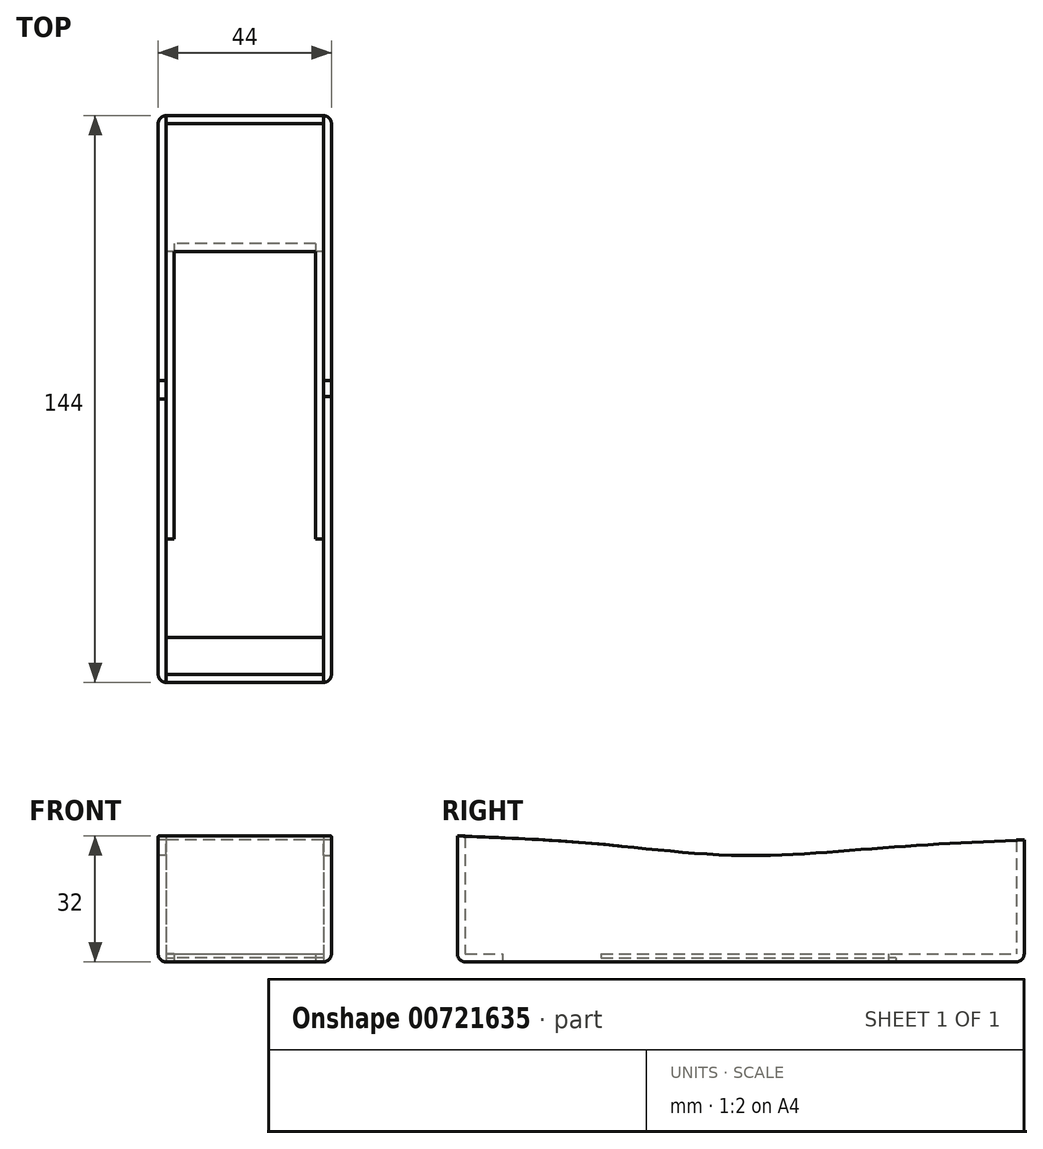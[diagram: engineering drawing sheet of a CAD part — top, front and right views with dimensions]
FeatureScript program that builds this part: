
annotation { "Feature Type Name" : "Feature", "Feature Type Description" : "" }
export const myFeature = defineFeature(function(context is Context, id is Id, definition is map)
    precondition{}
    {
        {
            var Q0;
            Q0=qCreatedBy(makeId("Top.planeOp"),FACE);
            var sketch = newSketch(context, id + "F0", { "sketchPlane" : qUnion([Q0])});
            skLineSegment(sketch, "E0.bottom", {"start": v(20, -70) * mm, "end": v(-20, -70) * mm});
            skLineSegment(sketch, "E0.top", {"start": v(20, 70) * mm, "end": v(-20, 70) * mm});
            skLineSegment(sketch, "E0.left", {"start": v(20, -70) * mm, "end": v(20, 70) * mm});
            skLineSegment(sketch, "E0.right", {"start": v(-20, -70) * mm, "end": v(-20, 70) * mm});
            skPoint(sketch, "E0.middle", {"position": v(0, 0) * mm});
            skLineSegment(sketch, "E1.bottom", {"start": v(22, -72) * mm, "end": v(-22, -72) * mm});
            skLineSegment(sketch, "E1.top", {"start": v(22, 72) * mm, "end": v(-22, 72) * mm});
            skLineSegment(sketch, "E1.left", {"start": v(22, -72) * mm, "end": v(22, 72) * mm});
            skLineSegment(sketch, "E1.right", {"start": v(-22, -72) * mm, "end": v(-22, 72) * mm});
            skSolve(sketch);
        }
        {
            var Q0;
            Q0=makeQuery(id+"F0.imprint","IMPRINT",FACE,{"disambiguationData":[TD([[makeQuery(id+"F0.imprint","IMPRINT",EDGE,{"derivedFrom":sQuery(id+"F0.wireOp",EDGE,"E0.bottom")}),1.0]])]});
            var Q1;
            Q1=makeQuery(id+"F0.imprint","IMPRINT",FACE,{"disambiguationData":[TD([[makeQuery(id+"F0.imprint","IMPRINT",EDGE,{"derivedFrom":sQuery(id+"F0.wireOp",EDGE,"E0.bottom")}),-1.0]])]});
            extrude(context, id + "F1", {"entities" : qUnion([Q0, Q1]), "oppositeDirection" : true, "depth" : 2 * mm, "offsetDistance" : 25 * mm});
        }
        {
            var Q0;
            Q0=makeQuery(id+"F0.imprint","IMPRINT",FACE,{"disambiguationData":[TD([[makeQuery(id+"F0.imprint","IMPRINT",EDGE,{"derivedFrom":sQuery(id+"F0.wireOp",EDGE,"E0.bottom")}),1.0]])]});
            extrude(context, id + "F2", {"entities" : qUnion([Q0]), "operationType" : NewBodyOperationType.ADD, "depth" : 25 * mm, "offsetDistance" : 25 * mm});
        }
        {
            var Q0;
            {var subQ0=sQuery(id+"F0.wireOp",EDGE,"E1.left");Q0=makeQuery(id+"F2.boolean.opBoolean","MERGE",FACE,{"derivedFrom":[makeQuery(id+"F1.opExtrude","SWEPT_FACE",FACE,{"disambiguationData":[OSD([subQ0])]}),makeQuery(id+"F2.opExtrude","SWEPT_FACE",FACE,{"disambiguationData":[OSD([subQ0])]})]});}
            var sketch = newSketch(context, id + "F3", { "sketchPlane" : qUnion([Q0])});
            skLineSegment(sketch, "E2", {"start": v(-72, 25) * mm, "end": v(-72, 30) * mm});
            skLineSegment(sketch, "E3", {"start": v(72, 25) * mm, "end": v(72, 29) * mm});
            skLineSegment(sketch, "E4", {"start": v(0, 25) * mm, "end": v(0, 25.01) * mm, "construction": true});
            skLineSegment(sketch, "E5", {"start": v(-36.5, 25) * mm, "end": v(-36.5, 28) * mm, "construction": true});
            skLineSegment(sketch, "E6", {"start": v(36.5, 25) * mm, "end": v(36.5, 27) * mm, "construction": true});
            skFitSpline(sketch, "E7", {"points": [v(-72, 30) * mm, v(-36.5, 28) * mm, v(0, 25.01) * mm, v(36.5, 27) * mm, v(72, 29) * mm], "startDerivative": vector(142.08, -5.52) * mm, "endDerivative": vector(142.02, 6.52) * mm});
            skSolve(sketch);
        }
        {
            var Q0;
            {var subQ0=sQuery(id+"F0.wireOp",EDGE,"E1.right");Q0=makeQuery(id+"F2.boolean.opBoolean","MERGE",FACE,{"derivedFrom":[makeQuery(id+"F1.opExtrude","SWEPT_FACE",FACE,{"disambiguationData":[OSD([subQ0])]}),makeQuery(id+"F2.opExtrude","SWEPT_FACE",FACE,{"disambiguationData":[OSD([subQ0])]})]});}
            var sketch = newSketch(context, id + "F4", { "sketchPlane" : qUnion([Q0])});
            skLineSegment(sketch, "E8", {"start": v(72, 25) * mm, "end": v(72, 30) * mm});
            skLineSegment(sketch, "E9", {"start": v(-72, 25) * mm, "end": v(-72, 29) * mm});
            skLineSegment(sketch, "E10", {"start": v(-36.5, 25) * mm, "end": v(-36.5, 27) * mm, "construction": true});
            skLineSegment(sketch, "E11", {"start": v(36.5, 25) * mm, "end": v(36.5, 28) * mm, "construction": true});
            skLineSegment(sketch, "E12", {"start": v(0, 25) * mm, "end": v(0, 25.01) * mm});
            skFitSpline(sketch, "E13", {"points": [v(-72, 29) * mm, v(-36.5, 27) * mm, v(0, 25.01) * mm, v(36.5, 28) * mm, v(72, 30) * mm], "startDerivative": vector(142.02, -6.52) * mm, "endDerivative": vector(142.08, 5.52) * mm});
            skSolve(sketch);
        }
        {
            var Q0;
            {var subQ0=sQuery(id+"F3.wireOp",EDGE,"E3");Q0=makeQuery(id+"F3.imprint","IMPRINT",FACE,{"disambiguationData":[TD([[makeQuery(id+"F3.imprint","IMPRINT",EDGE,{"derivedFrom":subQ0}),1.0]])]});}
            var Q1;
            {var subQ0=sQuery(id+"F3.wireOp",EDGE,"E2");Q1=makeQuery(id+"F3.imprint","IMPRINT",FACE,{"disambiguationData":[TD([[makeQuery(id+"F3.imprint","IMPRINT",EDGE,{"derivedFrom":subQ0}),-1.0]])]});}
            extrude(context, id + "F5", {"entities" : qUnion([Q0, Q1]), "operationType" : NewBodyOperationType.ADD, "oppositeDirection" : true, "depth" : 2 * mm, "offsetDistance" : 25 * mm});
        }
        {
            var Q0;
            Q0 = qSketchRegion(id + "F4", true);
            var Q1;
            {var subQ0=sQuery(id+"F4.wireOp",EDGE,"E9");Q1=makeQuery(id+"F4.imprint","IMPRINT",FACE,{"disambiguationData":[TD([[makeQuery(id+"F4.imprint","IMPRINT",EDGE,{"derivedFrom":subQ0}),-1.0]])]});}
            var Q2;
            {var subQ0=sQuery(id+"F4.wireOp",EDGE,"E8");Q2=makeQuery(id+"F4.imprint","IMPRINT",FACE,{"disambiguationData":[TD([[makeQuery(id+"F4.imprint","IMPRINT",EDGE,{"derivedFrom":subQ0}),1.0]])]});}
            extrude(context, id + "F6", {"entities" : qUnion([Q0, Q1, Q2]), "operationType" : NewBodyOperationType.ADD, "oppositeDirection" : true, "depth" : 2 * mm, "offsetDistance" : 25 * mm});
        }
        {
            var Q0;
            {var subQ2=sQuery(id+"F0.wireOp",EDGE,"E1.right");var subQ3=sQuery(id+"F0.wireOp",EDGE,"E0.right");var subQ7=sQuery(id+"F0.wireOp",EDGE,"E1.bottom");var subQ11=sQuery(id+"F0.wireOp",EDGE,"E1.left");var subQ13=makeQuery(id+"F1.opExtrude","SWEPT_FACE",FACE,{"disambiguationData":[OSD([subQ7])]});var subQ15=sQuery(id+"F0.wireOp",EDGE,"E0.left");var subQ17=sQuery(id+"F0.wireOp",EDGE,"E0.bottom");var subQ19=sQuery(id+"F0.wireOp",EDGE,"E0.top");var subQ20=sQuery(id+"F0.wireOp",EDGE,"E1.top");Q0=makeQuery(id+"F6.boolean.opBoolean","SPLIT",FACE,{"disambiguationData":[TD([subQ13])],"derivedFrom":makeQuery(id+"F5.boolean.opBoolean","SPLIT",FACE,{"disambiguationData":[TD([subQ13])],"derivedFrom":makeQuery(id+"F2.opExtrude","CAP_FACE",FACE,{"disambiguationData":[OSD([subQ17,subQ19,subQ15,subQ3,subQ7,subQ20,subQ11,subQ2])],"isStart":false})})});}
            extrude(context, id + "F7", {"entities" : qUnion([Q0]), "operationType" : NewBodyOperationType.ADD, "depth" : 5 * mm, "offsetDistance" : 25 * mm});
        }
        {
            var Q0;
            {var subQ2=sQuery(id+"F0.wireOp",EDGE,"E1.right");var subQ3=sQuery(id+"F0.wireOp",EDGE,"E0.right");var subQ7=sQuery(id+"F0.wireOp",EDGE,"E1.left");var subQ9=sQuery(id+"F0.wireOp",EDGE,"E1.top");var subQ11=makeQuery(id+"F1.opExtrude","SWEPT_FACE",FACE,{"disambiguationData":[OSD([subQ9])]});var subQ12=sQuery(id+"F0.wireOp",EDGE,"E0.top");var subQ16=sQuery(id+"F0.wireOp",EDGE,"E0.left");var subQ19=sQuery(id+"F0.wireOp",EDGE,"E1.bottom");var subQ20=sQuery(id+"F0.wireOp",EDGE,"E0.bottom");Q0=makeQuery(id+"F6.boolean.opBoolean","SPLIT",FACE,{"disambiguationData":[TD([subQ11])],"derivedFrom":makeQuery(id+"F5.boolean.opBoolean","SPLIT",FACE,{"disambiguationData":[TD([makeQuery(id+"F1.opExtrude","SWEPT_FACE",FACE,{"disambiguationData":[OSD([subQ19])]})])],"derivedFrom":makeQuery(id+"F2.opExtrude","CAP_FACE",FACE,{"disambiguationData":[OSD([subQ20,subQ12,subQ16,subQ3,subQ19,subQ9,subQ7,subQ2])],"isStart":false})})});}
            extrude(context, id + "F8", {"entities" : qUnion([Q0]), "operationType" : NewBodyOperationType.ADD, "depth" : 4 * mm, "offsetDistance" : 25 * mm});
        }
        {
            var Q0;
            Q0=makeQuery(id+"F1.opExtrude","CAP_FACE",FACE,{"disambiguationData":[OSD([sQuery(id+"F0.wireOp",EDGE,"E1.bottom"),sQuery(id+"F0.wireOp",EDGE,"E1.top"),sQuery(id+"F0.wireOp",EDGE,"E1.left"),sQuery(id+"F0.wireOp",EDGE,"E1.right")])],"isStart":false});
            var sketch = newSketch(context, id + "F9", { "sketchPlane" : qUnion([Q0])});
            skLineSegment(sketch, "E14", {"start": v(0, 70) * mm, "end": v(0, 35.56) * mm, "construction": true});
            skLineSegment(sketch, "E15.bottom", {"start": v(20, 60.52) * mm, "end": v(-20, 60.52) * mm});
            skLineSegment(sketch, "E15.top", {"start": v(20, -39.48) * mm, "end": v(-20, -39.48) * mm});
            skLineSegment(sketch, "E15.left", {"start": v(20, 60.52) * mm, "end": v(20, -39.48) * mm});
            skLineSegment(sketch, "E15.right", {"start": v(-20, 60.52) * mm, "end": v(-20, -39.48) * mm});
            skLineSegment(sketch, "E16.bottom", {"start": v(20, -39.48) * mm, "end": v(18, -39.48) * mm});
            skLineSegment(sketch, "E16.top", {"start": v(20, 35.52) * mm, "end": v(18, 35.52) * mm});
            skLineSegment(sketch, "E16.left", {"start": v(20, -39.48) * mm, "end": v(20, 35.52) * mm});
            skLineSegment(sketch, "E16.right", {"start": v(18, -39.48) * mm, "end": v(18, 35.52) * mm});
            skLineSegment(sketch, "E17.bottom", {"start": v(-20, -39.48) * mm, "end": v(-18, -39.48) * mm});
            skLineSegment(sketch, "E17.top", {"start": v(-20, 35.52) * mm, "end": v(-18, 35.52) * mm});
            skLineSegment(sketch, "E17.left", {"start": v(-20, -39.48) * mm, "end": v(-20, 35.52) * mm});
            skLineSegment(sketch, "E17.right", {"start": v(-18, -39.48) * mm, "end": v(-18, 35.52) * mm});
            skLineSegment(sketch, "E18.top", {"start": v(20, -37.48) * mm, "end": v(-20, -37.48) * mm});
            skLineSegment(sketch, "E18.left", {"start": v(20, -39.48) * mm, "end": v(20, -37.48) * mm});
            skLineSegment(sketch, "E18.right", {"start": v(-20, -39.48) * mm, "end": v(-20, -37.48) * mm});
            skSolve(sketch);
        }
        {
            var Q0;
            Q0=makeQuery(id+"F9.imprint","IMPRINT",FACE,{"disambiguationData":[TD([[makeQuery(id+"F9.imprint","IMPRINT",EDGE,{"derivedFrom":sQuery(id+"F9.wireOp",EDGE,"E15.bottom")}),1.0]])]});
            extrude(context, id + "F10", {"entities" : qUnion([Q0]), "operationType" : NewBodyOperationType.REMOVE, "endBound" : BoundingType.THROUGH_ALL, "oppositeDirection" : true, "depth" : 25 * mm, "offsetDistance" : 25 * mm});
        }
        {
            var Q0;
            {var subQ0=sQuery(id+"F9.wireOp",EDGE,"E15.top");var subQ1=sQuery(id+"F9.wireOp",EDGE,"E16.right");var subQ2=makeQuery(id+"F9.imprint","INTERSECT",VERTEX,{"derivedFrom":[subQ1,subQ0]});Q0=makeQuery(id+"F9.imprint","IMPRINT",FACE,{"disambiguationData":[TD([[makeQuery(id+"F9.imprint","IMPRINT",EDGE,{"disambiguationData":[TD([[subQ2,-1.0]])],"derivedFrom":subQ1}),1.0]])]});}
            var Q1;
            {var subQ5=sQuery(id+"F9.wireOp",EDGE,"E18.right");Q1=makeQuery(id+"F9.imprint","IMPRINT",FACE,{"disambiguationData":[TD([[makeQuery(id+"F9.imprint","IMPRINT",EDGE,{"derivedFrom":subQ5}),-1.0]])]});}
            var Q2;
            {var subQ0=sQuery(id+"F9.wireOp",EDGE,"E17.top");Q2=makeQuery(id+"F9.imprint","IMPRINT",FACE,{"disambiguationData":[TD([[makeQuery(id+"F9.imprint","IMPRINT",EDGE,{"derivedFrom":subQ0}),-1.0]])]});}
            var Q3;
            {var subQ5=sQuery(id+"F9.wireOp",EDGE,"E18.left");Q3=makeQuery(id+"F9.imprint","IMPRINT",FACE,{"disambiguationData":[TD([[makeQuery(id+"F9.imprint","IMPRINT",EDGE,{"derivedFrom":subQ5}),1.0]])]});}
            var Q4;
            {var subQ0=sQuery(id+"F9.wireOp",EDGE,"E16.top");Q4=makeQuery(id+"F9.imprint","IMPRINT",FACE,{"disambiguationData":[TD([[makeQuery(id+"F9.imprint","IMPRINT",EDGE,{"derivedFrom":subQ0}),1.0]])]});}
            extrude(context, id + "F11", {"entities" : qUnion([Q0, Q1, Q2, Q3, Q4]), "operationType" : NewBodyOperationType.REMOVE, "oppositeDirection" : true, "depth" : 1 * mm, "offsetDistance" : 25 * mm});
        }
        {
            var Q0;
            Q0=makeQuery(id+"F1.opExtrude","CAP_EDGE",EDGE,{"disambiguationData":[OSD([sQuery(id+"F0.wireOp",EDGE,"E1.bottom")])],"isStart":false});
            var Q1;
            Q1=makeQuery(id+"F1.opExtrude","CAP_EDGE",EDGE,{"disambiguationData":[OSD([sQuery(id+"F0.wireOp",EDGE,"E1.right")])],"isStart":false});
            var Q2;
            Q2=makeQuery(id+"F1.opExtrude","CAP_EDGE",EDGE,{"disambiguationData":[OSD([sQuery(id+"F0.wireOp",EDGE,"E1.left")])],"isStart":false});
            var Q3;
            {var subQ0=sQuery(id+"F0.wireOp",EDGE,"E1.right");var subQ1=sQuery(id+"F0.wireOp",EDGE,"E1.bottom");Q3=makeQuery(id+"F6.boolean.opBoolean","MERGE",EDGE,{"derivedFrom":[makeQuery(id+"F2.boolean.opBoolean","MERGE",EDGE,{"derivedFrom":[makeQuery(id+"F1.opExtrude","SWEPT_EDGE",EDGE,{"disambiguationData":[OSD([subQ1,subQ0])]}),makeQuery(id+"F2.opExtrude","SWEPT_EDGE",EDGE,{"disambiguationData":[OSD([subQ1,subQ0])]})]}),makeQuery(id+"F6.opExtrude","CAP_EDGE",EDGE,{"disambiguationData":[OSD([sQuery(id+"F4.wireOp",EDGE,"E8")])],"isStart":true})]});}
            var Q4;
            {var subQ0=sQuery(id+"F0.wireOp",EDGE,"E1.left");var subQ1=sQuery(id+"F0.wireOp",EDGE,"E1.bottom");Q4=makeQuery(id+"F5.boolean.opBoolean","MERGE",EDGE,{"derivedFrom":[makeQuery(id+"F2.boolean.opBoolean","MERGE",EDGE,{"derivedFrom":[makeQuery(id+"F1.opExtrude","SWEPT_EDGE",EDGE,{"disambiguationData":[OSD([subQ1,subQ0])]}),makeQuery(id+"F2.opExtrude","SWEPT_EDGE",EDGE,{"disambiguationData":[OSD([subQ1,subQ0])]})]}),makeQuery(id+"F5.opExtrude","CAP_EDGE",EDGE,{"disambiguationData":[OSD([sQuery(id+"F3.wireOp",EDGE,"E2")])],"isStart":true})]});}
            var Q5;
            Q5=makeQuery(id+"F1.opExtrude","CAP_EDGE",EDGE,{"disambiguationData":[OSD([sQuery(id+"F0.wireOp",EDGE,"E1.top")])],"isStart":false});
            var Q6;
            {var subQ0=sQuery(id+"F0.wireOp",EDGE,"E1.right");var subQ1=sQuery(id+"F0.wireOp",EDGE,"E1.top");Q6=makeQuery(id+"F6.boolean.opBoolean","MERGE",EDGE,{"derivedFrom":[makeQuery(id+"F2.boolean.opBoolean","MERGE",EDGE,{"derivedFrom":[makeQuery(id+"F1.opExtrude","SWEPT_EDGE",EDGE,{"disambiguationData":[OSD([subQ1,subQ0])]}),makeQuery(id+"F2.opExtrude","SWEPT_EDGE",EDGE,{"disambiguationData":[OSD([subQ1,subQ0])]})]}),makeQuery(id+"F6.opExtrude","CAP_EDGE",EDGE,{"disambiguationData":[OSD([sQuery(id+"F4.wireOp",EDGE,"E9")])],"isStart":true})]});}
            var Q7;
            {var subQ0=sQuery(id+"F0.wireOp",EDGE,"E1.left");var subQ1=sQuery(id+"F0.wireOp",EDGE,"E1.top");Q7=makeQuery(id+"F5.boolean.opBoolean","MERGE",EDGE,{"derivedFrom":[makeQuery(id+"F2.boolean.opBoolean","MERGE",EDGE,{"derivedFrom":[makeQuery(id+"F1.opExtrude","SWEPT_EDGE",EDGE,{"disambiguationData":[OSD([subQ1,subQ0])]}),makeQuery(id+"F2.opExtrude","SWEPT_EDGE",EDGE,{"disambiguationData":[OSD([subQ1,subQ0])]})]}),makeQuery(id+"F5.opExtrude","CAP_EDGE",EDGE,{"disambiguationData":[OSD([sQuery(id+"F3.wireOp",EDGE,"E3")])],"isStart":true})]});}
            fillet(context, id + "F12", {"entities" : qUnion([Q0, Q1, Q2, Q3, Q4, Q5, Q6, Q7]), "radius" : 2 * mm, "tangentPropagation" : true, "allowEdgeOverflow" : false});
        }
    });
